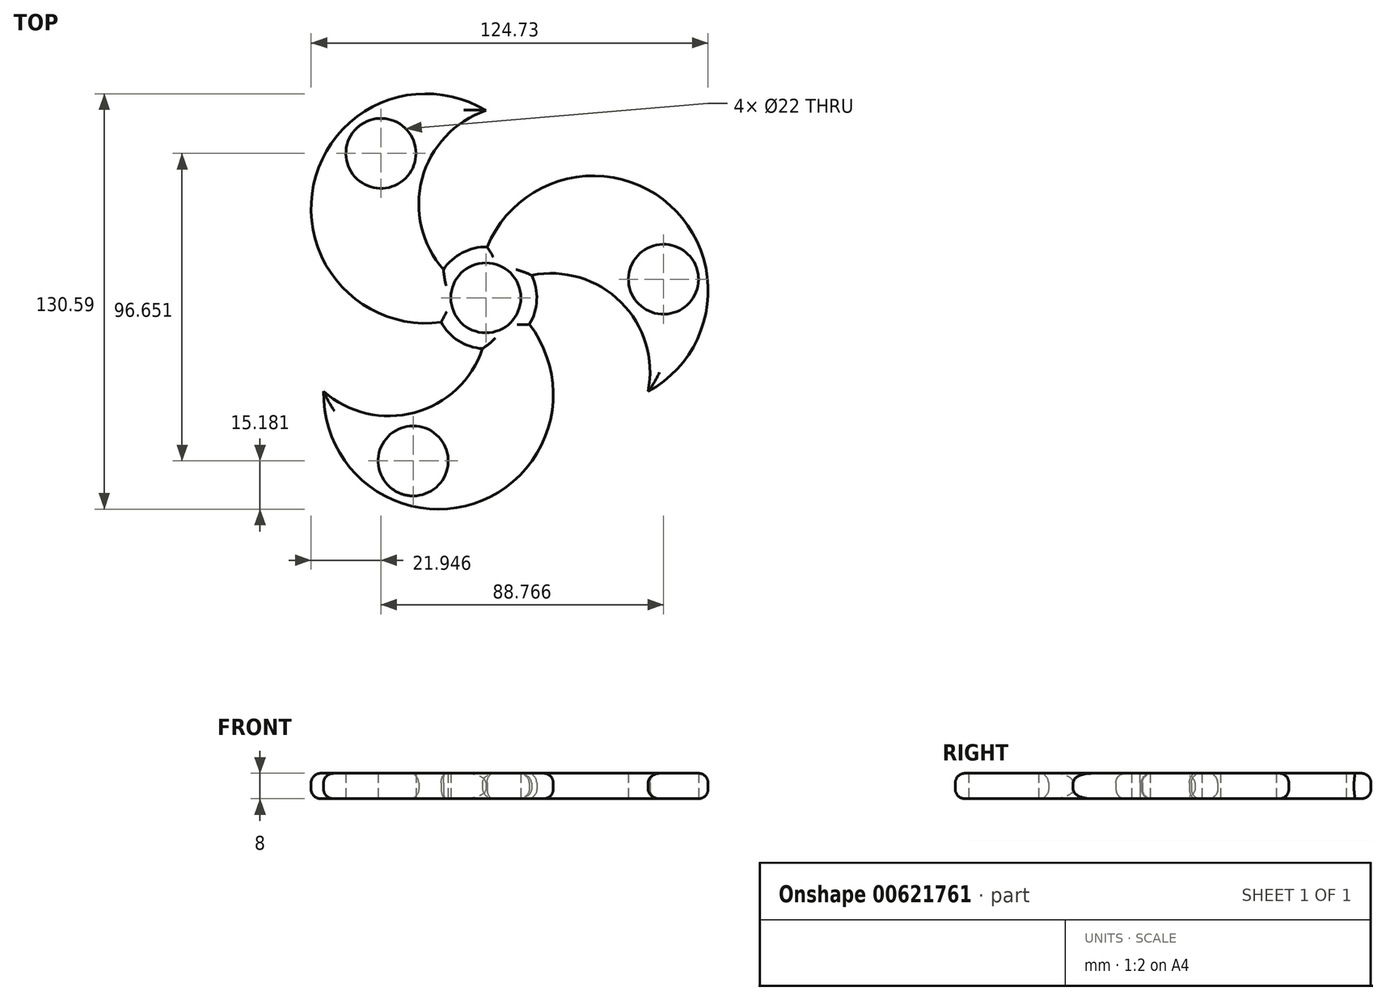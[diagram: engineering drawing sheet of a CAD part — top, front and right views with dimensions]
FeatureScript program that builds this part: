
annotation { "Feature Type Name" : "Feature", "Feature Type Description" : "" }
export const myFeature = defineFeature(function(context is Context, id is Id, definition is map)
    precondition{}
    {
        {
            var Q0;
            Q0=qCreatedBy(makeId("Top.planeOp"),FACE);
            var sketch = newSketch(context, id + "F0", { "sketchPlane" : qUnion([Q0])});
            skCircle(sketch, "E0", {"center": v(0, 0) * mm, "radius": 11 * mm});
            skCircle(sketch, "E1", {"center": v(0, 0) * mm, "radius": 58.85 * mm});
            skArc(sketch, "E2", {"start": v(0, 58.85) * mm, "mid": v(-21.08, 29.43) * mm, "end": v(0, 0) * mm});
            skArc(sketch, "E3", {"start": v(50.97, -29.43) * mm, "mid": v(36.02, 3.54) * mm, "end": v(0, 0) * mm});
            skArc(sketch, "E4", {"start": v(-50.97, -29.43) * mm, "mid": v(-14.94, -32.97) * mm, "end": v(0, 0) * mm});
            skArc(sketch, "E5", {"start": v(0, 58.85) * mm, "mid": v(-54.36, 21.8) * mm, "end": v(9.43, 5.67) * mm});
            skArc(sketch, "E6", {"start": v(-50.97, -29.43) * mm, "mid": v(8.3, -57.97) * mm, "end": v(-9.62, 5.33) * mm});
            skArc(sketch, "E7", {"start": v(50.97, -29.43) * mm, "mid": v(46.05, 36.18) * mm, "end": v(0.2, -11) * mm});
            skCircle(sketch, "E8", {"center": v(0, 0) * mm, "radius": 16 * mm});
            skCircle(sketch, "E9", {"center": v(-32.96, 45.4) * mm, "radius": 11 * mm});
            skCircle(sketch, "E10.1.0", {"center": v(-22.84, -51.25) * mm, "radius": 11 * mm});
            skCircle(sketch, "E10.2.0", {"center": v(55.8, 5.85) * mm, "radius": 11 * mm});
            skSolve(sketch);
        }
        {
            var Q0;
            {var subQ0=sQuery(id+"F0.wireOp",EDGE,"E5");var subQ1=sQuery(id+"F0.wireOp",EDGE,"E1");var subQ5=makeQuery(id+"F0.imprint","INTERSECT",VERTEX,{"derivedFrom":[subQ1,subQ0]});Q0=makeQuery(id+"F0.imprint","IMPRINT",FACE,{"disambiguationData":[TD([[makeQuery(id+"F0.imprint","IMPRINT",EDGE,{"disambiguationData":[TD([[subQ5,1.0]])],"derivedFrom":subQ1}),-1.0]])]});}
            var Q1;
            {var subQ0=sQuery(id+"F0.wireOp",EDGE,"E5");var subQ1=sQuery(id+"F0.wireOp",EDGE,"E1");var subQ2=makeQuery(id+"F0.imprint","INTERSECT",VERTEX,{"derivedFrom":[subQ1,subQ0]});Q1=makeQuery(id+"F0.imprint","IMPRINT",FACE,{"disambiguationData":[TD([[makeQuery(id+"F0.imprint","IMPRINT",EDGE,{"disambiguationData":[TD([[subQ2,1.0]])],"derivedFrom":subQ1}),1.0]])]});}
            var Q2;
            {var subQ0=sQuery(id+"F0.wireOp",EDGE,"E7");var subQ1=sQuery(id+"F0.wireOp",EDGE,"E1");var subQ2=makeQuery(id+"F0.imprint","INTERSECT",VERTEX,{"derivedFrom":[subQ1,subQ0]});Q2=makeQuery(id+"F0.imprint","IMPRINT",FACE,{"disambiguationData":[TD([[makeQuery(id+"F0.imprint","IMPRINT",EDGE,{"disambiguationData":[TD([[subQ2,1.0]])],"derivedFrom":subQ1}),1.0]])]});}
            var Q3;
            {var subQ0=sQuery(id+"F0.wireOp",EDGE,"E7");var subQ1=sQuery(id+"F0.wireOp",EDGE,"E1");var subQ2=makeQuery(id+"F0.imprint","INTERSECT",VERTEX,{"derivedFrom":[subQ1,subQ0]});Q3=makeQuery(id+"F0.imprint","IMPRINT",FACE,{"disambiguationData":[TD([[makeQuery(id+"F0.imprint","IMPRINT",EDGE,{"disambiguationData":[TD([[subQ2,1.0]])],"derivedFrom":subQ1}),-1.0]])]});}
            var Q4;
            {var subQ0=sQuery(id+"F0.wireOp",EDGE,"E6");var subQ1=sQuery(id+"F0.wireOp",EDGE,"E1");var subQ2=makeQuery(id+"F0.imprint","INTERSECT",VERTEX,{"derivedFrom":[subQ1,subQ0]});Q4=makeQuery(id+"F0.imprint","IMPRINT",FACE,{"disambiguationData":[TD([[makeQuery(id+"F0.imprint","IMPRINT",EDGE,{"disambiguationData":[TD([[subQ2,1.0]])],"derivedFrom":subQ1}),1.0]])]});}
            var Q5;
            {var subQ0=sQuery(id+"F0.wireOp",EDGE,"E6");var subQ1=sQuery(id+"F0.wireOp",EDGE,"E1");var subQ5=makeQuery(id+"F0.imprint","INTERSECT",VERTEX,{"derivedFrom":[subQ1,subQ0]});Q5=makeQuery(id+"F0.imprint","IMPRINT",FACE,{"disambiguationData":[TD([[makeQuery(id+"F0.imprint","IMPRINT",EDGE,{"disambiguationData":[TD([[subQ5,1.0]])],"derivedFrom":subQ1}),-1.0]])]});}
            var Q6;
            {var subQ1=sQuery(id+"F0.wireOp",EDGE,"E0");var subQ3=sQuery(id+"F0.wireOp",EDGE,"E5");var subQ4=makeQuery(id+"F0.imprint","INTERSECT",VERTEX,{"derivedFrom":[subQ1,subQ3]});Q6=makeQuery(id+"F0.imprint","IMPRINT",FACE,{"disambiguationData":[TD([[makeQuery(id+"F0.imprint","IMPRINT",EDGE,{"disambiguationData":[TD([[subQ4,1.0]])],"derivedFrom":subQ3}),-1.0]])]});}
            var Q7;
            {var subQ1=sQuery(id+"F0.wireOp",EDGE,"E0");var subQ3=sQuery(id+"F0.wireOp",EDGE,"E5");var subQ4=makeQuery(id+"F0.imprint","INTERSECT",VERTEX,{"derivedFrom":[subQ1,subQ3]});Q7=makeQuery(id+"F0.imprint","IMPRINT",FACE,{"disambiguationData":[TD([[makeQuery(id+"F0.imprint","IMPRINT",EDGE,{"disambiguationData":[TD([[subQ4,1.0]])],"derivedFrom":subQ3}),1.0]])]});}
            var Q8;
            {var subQ1=sQuery(id+"F0.wireOp",EDGE,"E0");var subQ3=sQuery(id+"F0.wireOp",EDGE,"E7");var subQ4=makeQuery(id+"F0.imprint","INTERSECT",VERTEX,{"derivedFrom":[subQ1,subQ3]});Q8=makeQuery(id+"F0.imprint","IMPRINT",FACE,{"disambiguationData":[TD([[makeQuery(id+"F0.imprint","IMPRINT",EDGE,{"disambiguationData":[TD([[subQ4,1.0]])],"derivedFrom":subQ3}),-1.0]])]});}
            var Q9;
            {var subQ1=sQuery(id+"F0.wireOp",EDGE,"E0");var subQ3=sQuery(id+"F0.wireOp",EDGE,"E7");var subQ4=makeQuery(id+"F0.imprint","INTERSECT",VERTEX,{"derivedFrom":[subQ1,subQ3]});Q9=makeQuery(id+"F0.imprint","IMPRINT",FACE,{"disambiguationData":[TD([[makeQuery(id+"F0.imprint","IMPRINT",EDGE,{"disambiguationData":[TD([[subQ4,1.0]])],"derivedFrom":subQ3}),1.0]])]});}
            var Q10;
            {var subQ1=sQuery(id+"F0.wireOp",EDGE,"E0");var subQ3=sQuery(id+"F0.wireOp",EDGE,"E6");var subQ4=makeQuery(id+"F0.imprint","INTERSECT",VERTEX,{"derivedFrom":[subQ1,subQ3]});Q10=makeQuery(id+"F0.imprint","IMPRINT",FACE,{"disambiguationData":[TD([[makeQuery(id+"F0.imprint","IMPRINT",EDGE,{"disambiguationData":[TD([[subQ4,1.0]])],"derivedFrom":subQ3}),-1.0]])]});}
            var Q11;
            {var subQ1=sQuery(id+"F0.wireOp",EDGE,"E0");var subQ3=sQuery(id+"F0.wireOp",EDGE,"E6");var subQ4=makeQuery(id+"F0.imprint","INTERSECT",VERTEX,{"derivedFrom":[subQ1,subQ3]});Q11=makeQuery(id+"F0.imprint","IMPRINT",FACE,{"disambiguationData":[TD([[makeQuery(id+"F0.imprint","IMPRINT",EDGE,{"disambiguationData":[TD([[subQ4,1.0]])],"derivedFrom":subQ3}),1.0]])]});}
            extrude(context, id + "F1", {"entities" : qUnion([Q0, Q1, Q2, Q3, Q4, Q5, Q6, Q7, Q8, Q9, Q10, Q11]), "depth" : 8 * mm, "offsetDistance" : 25 * mm});
        }
        {
            var Q0;
            Q0=makeQuery(id+"F1.opExtrude","CAP_EDGE",EDGE,{"disambiguationData":[OSD([sQuery(id+"F0.wireOp",EDGE,"E6")])],"isStart":false});
            var Q1;
            {var subQ0=sQuery(id+"F0.wireOp",EDGE,"E8");Q1=makeQuery(id+"F1.opExtrude","CAP_EDGE",EDGE,{"disambiguationData":[OSD([subQ0]),TDD([makeQuery(id+"F0.imprint","IMPRINT",EDGE,{"disambiguationData":[TD([[makeQuery(id+"F0.imprint","INTERSECT",VERTEX,{"derivedFrom":[sQuery(id+"F0.wireOp",EDGE,"E3"),subQ0]}),1.0]])],"derivedFrom":subQ0})])],"isStart":false});}
            var Q2;
            Q2=makeQuery(id+"F1.opExtrude","CAP_EDGE",EDGE,{"disambiguationData":[OSD([sQuery(id+"F0.wireOp",EDGE,"E3")])],"isStart":false});
            var Q3;
            Q3=makeQuery(id+"F1.opExtrude","CAP_EDGE",EDGE,{"disambiguationData":[OSD([sQuery(id+"F0.wireOp",EDGE,"E7")])],"isStart":false});
            var Q4;
            {var subQ0=sQuery(id+"F0.wireOp",EDGE,"E8");Q4=makeQuery(id+"F1.opExtrude","CAP_EDGE",EDGE,{"disambiguationData":[OSD([subQ0]),TDD([makeQuery(id+"F0.imprint","IMPRINT",EDGE,{"disambiguationData":[TD([[makeQuery(id+"F0.imprint","INTERSECT",VERTEX,{"derivedFrom":[sQuery(id+"F0.wireOp",EDGE,"E2"),subQ0]}),1.0]])],"derivedFrom":subQ0})])],"isStart":false});}
            var Q5;
            Q5=makeQuery(id+"F1.opExtrude","CAP_EDGE",EDGE,{"disambiguationData":[OSD([sQuery(id+"F0.wireOp",EDGE,"E2")])],"isStart":false});
            var Q6;
            Q6=makeQuery(id+"F1.opExtrude","CAP_EDGE",EDGE,{"disambiguationData":[OSD([sQuery(id+"F0.wireOp",EDGE,"E5")])],"isStart":false});
            var Q7;
            {var subQ0=sQuery(id+"F0.wireOp",EDGE,"E8");Q7=makeQuery(id+"F1.opExtrude","CAP_EDGE",EDGE,{"disambiguationData":[OSD([subQ0]),TDD([makeQuery(id+"F0.imprint","IMPRINT",EDGE,{"disambiguationData":[TD([[makeQuery(id+"F0.imprint","INTERSECT",VERTEX,{"derivedFrom":[sQuery(id+"F0.wireOp",EDGE,"E4"),subQ0]}),1.0]])],"derivedFrom":subQ0})])],"isStart":false});}
            var Q8;
            Q8=makeQuery(id+"F1.opExtrude","CAP_EDGE",EDGE,{"disambiguationData":[OSD([sQuery(id+"F0.wireOp",EDGE,"E4")])],"isStart":false});
            var Q9;
            Q9=makeQuery(id+"F1.opExtrude","CAP_EDGE",EDGE,{"disambiguationData":[OSD([sQuery(id+"F0.wireOp",EDGE,"E5")])],"isStart":true});
            var Q10;
            {var subQ0=sQuery(id+"F0.wireOp",EDGE,"E8");Q10=makeQuery(id+"F1.opExtrude","CAP_EDGE",EDGE,{"disambiguationData":[OSD([subQ0]),TDD([makeQuery(id+"F0.imprint","IMPRINT",EDGE,{"disambiguationData":[TD([[makeQuery(id+"F0.imprint","INTERSECT",VERTEX,{"derivedFrom":[sQuery(id+"F0.wireOp",EDGE,"E4"),subQ0]}),1.0]])],"derivedFrom":subQ0})])],"isStart":true});}
            var Q11;
            Q11=makeQuery(id+"F1.opExtrude","CAP_EDGE",EDGE,{"disambiguationData":[OSD([sQuery(id+"F0.wireOp",EDGE,"E4")])],"isStart":true});
            var Q12;
            Q12=makeQuery(id+"F1.opExtrude","CAP_EDGE",EDGE,{"disambiguationData":[OSD([sQuery(id+"F0.wireOp",EDGE,"E6")])],"isStart":true});
            var Q13;
            {var subQ0=sQuery(id+"F0.wireOp",EDGE,"E8");Q13=makeQuery(id+"F1.opExtrude","CAP_EDGE",EDGE,{"disambiguationData":[OSD([subQ0]),TDD([makeQuery(id+"F0.imprint","IMPRINT",EDGE,{"disambiguationData":[TD([[makeQuery(id+"F0.imprint","INTERSECT",VERTEX,{"derivedFrom":[sQuery(id+"F0.wireOp",EDGE,"E3"),subQ0]}),1.0]])],"derivedFrom":subQ0})])],"isStart":true});}
            var Q14;
            Q14=makeQuery(id+"F1.opExtrude","CAP_EDGE",EDGE,{"disambiguationData":[OSD([sQuery(id+"F0.wireOp",EDGE,"E3")])],"isStart":true});
            var Q15;
            Q15=makeQuery(id+"F1.opExtrude","CAP_EDGE",EDGE,{"disambiguationData":[OSD([sQuery(id+"F0.wireOp",EDGE,"E7")])],"isStart":true});
            var Q16;
            Q16=makeQuery(id+"F1.opExtrude","CAP_EDGE",EDGE,{"disambiguationData":[OSD([sQuery(id+"F0.wireOp",EDGE,"E2")])],"isStart":true});
            var Q17;
            {var subQ0=sQuery(id+"F0.wireOp",EDGE,"E8");Q17=makeQuery(id+"F1.opExtrude","CAP_EDGE",EDGE,{"disambiguationData":[OSD([subQ0]),TDD([makeQuery(id+"F0.imprint","IMPRINT",EDGE,{"disambiguationData":[TD([[makeQuery(id+"F0.imprint","INTERSECT",VERTEX,{"derivedFrom":[sQuery(id+"F0.wireOp",EDGE,"E2"),subQ0]}),1.0]])],"derivedFrom":subQ0})])],"isStart":true});}
            fillet(context, id + "F2", {"entities" : qUnion([Q0, Q1, Q2, Q3, Q4, Q5, Q6, Q7, Q8, Q9, Q10, Q11, Q12, Q13, Q14, Q15, Q16, Q17]), "radius" : 3 * mm, "tangentPropagation" : true, "allowEdgeOverflow" : false});
        }
    });
